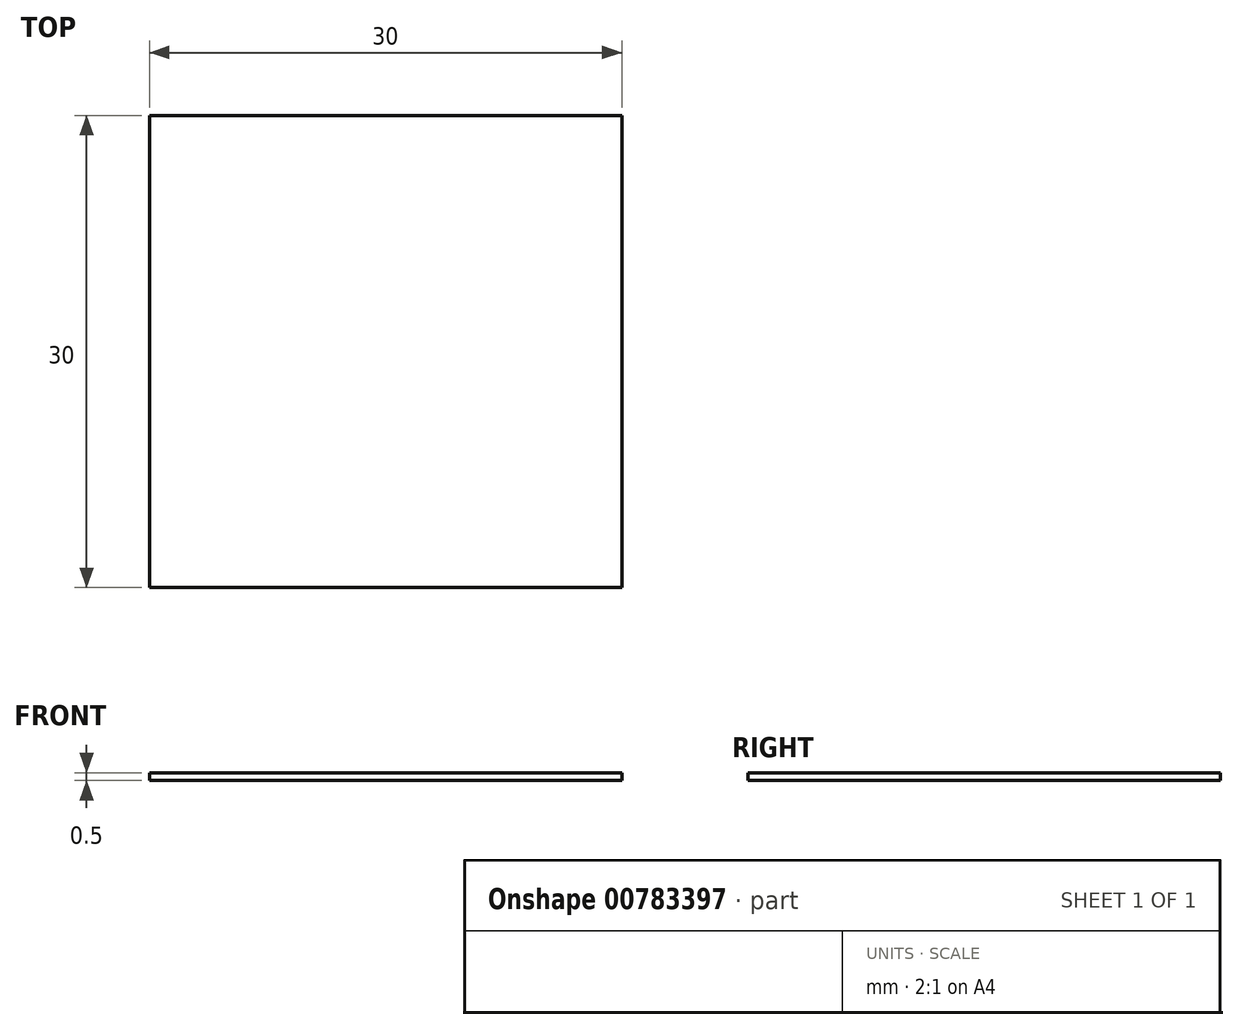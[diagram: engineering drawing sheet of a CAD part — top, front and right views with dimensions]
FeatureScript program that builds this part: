
annotation { "Feature Type Name" : "Feature", "Feature Type Description" : "" }
export const myFeature = defineFeature(function(context is Context, id is Id, definition is map)
    precondition{}
    {
        {
            var Q0;
            Q0=qCreatedBy(makeId("Top.planeOp"),FACE);
            var sketch = newSketch(context, id + "F0", { "sketchPlane" : qUnion([Q0])});
            skLineSegment(sketch, "E0.bottom", {"start": v(15, -15) * mm, "end": v(-15, -15) * mm});
            skLineSegment(sketch, "E0.top", {"start": v(15, 15) * mm, "end": v(-15, 15) * mm});
            skLineSegment(sketch, "E0.left", {"start": v(15, -15) * mm, "end": v(15, 15) * mm});
            skLineSegment(sketch, "E0.right", {"start": v(-15, -15) * mm, "end": v(-15, 15) * mm});
            skPoint(sketch, "E0.middle", {"position": v(0, 0) * mm});
            skSolve(sketch);
        }
        {
            var Q0;
            Q0=qSketchRegion(id+"F0",true);
            extrude(context, id + "F1", {"entities" : qUnion([Q0]), "depth" : 0.5 * mm, "offsetDistance" : 25.4 * mm});
        }
    });
